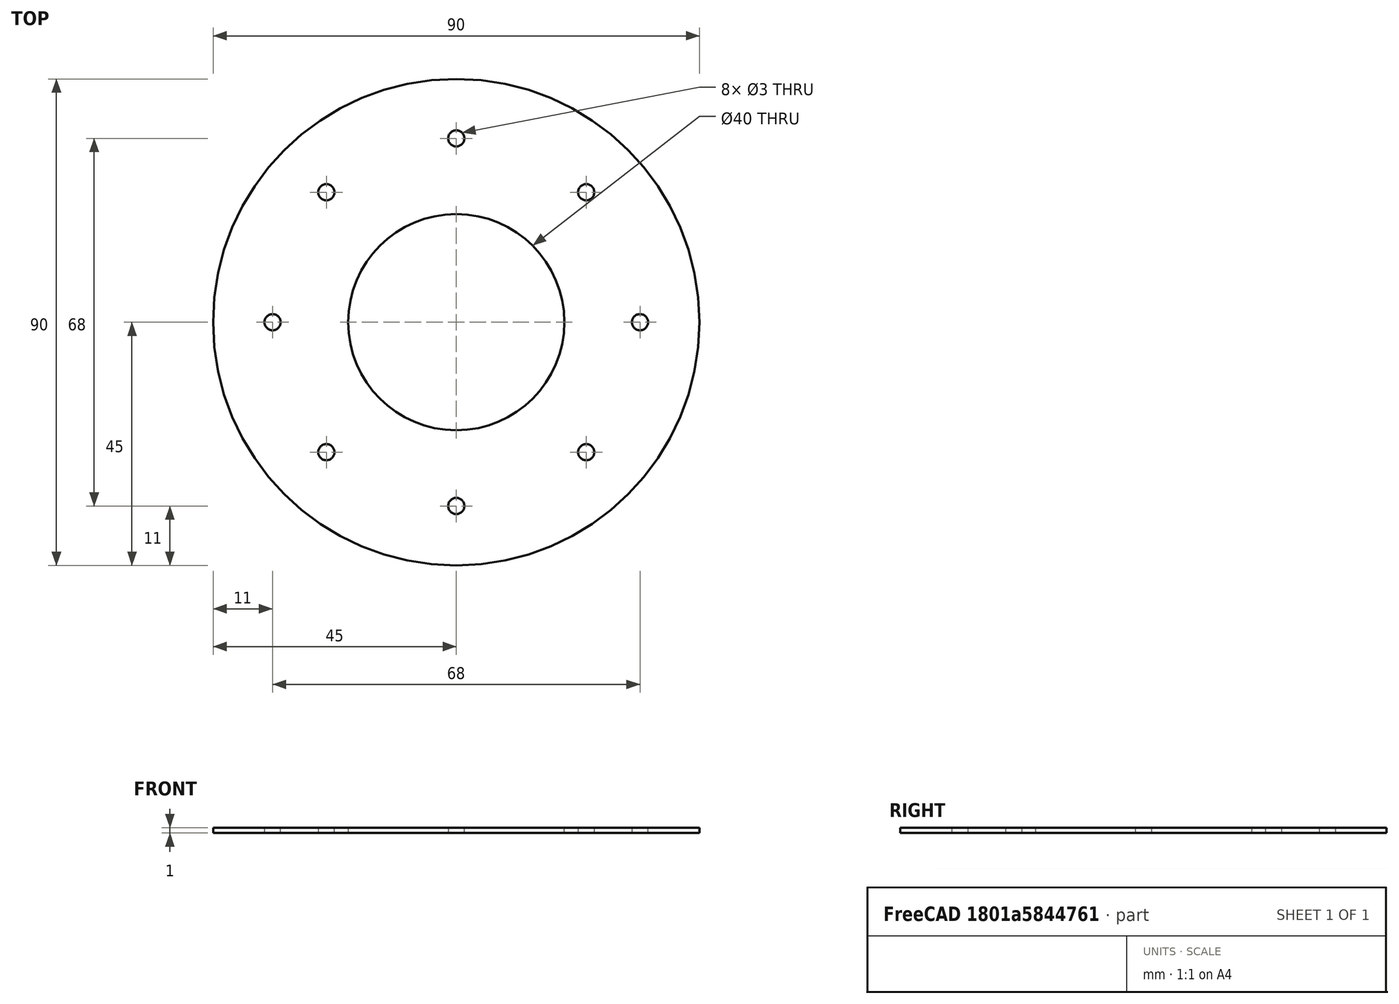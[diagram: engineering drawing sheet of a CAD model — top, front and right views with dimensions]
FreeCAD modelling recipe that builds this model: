
FCSTD DOCUMENT  (FreeCAD 0.20R29603 (Git))
Label: Rubber_Ring_I_LightDome
License: All rights reserved
LicenseURL: http://en.wikipedia.org/wiki/All_rights_reserved
objects: TechDraw::DrawViewDimension×4, App::DocumentObjectGroup×4, Sketcher::SketchObject×1, Part::Extrusion×1, TechDraw::DrawSVGTemplate×1, TechDraw::DrawViewPart×1, TechDraw::DrawViewAnnotation×1, TechDraw::DrawPage×1, App::Part×1
note: 2 computed .brp shape members not serialized (recipe doc carries the construction recipe); baked Part::Feature solids carry a one-line shape summary decoded from their .brp

FEATURE [Sketcher::SketchObject] Sketch
  FullyConstrained = false
  sketch-geometry (18):
    g0: Circle CenterX=0 CenterY=8e-16 CenterZ=0 NormalX=0 NormalY=0 NormalZ=1 AngleXU=0 Radius=20
    g1: LineSegment StartX=-70 StartY=70 StartZ=0 EndX=70 EndY=70 EndZ=0
    g2: LineSegment StartX=70 StartY=70 StartZ=0 EndX=70 EndY=-70 EndZ=0
    g3: LineSegment StartX=70 StartY=-70 StartZ=0 EndX=-70 EndY=-70 EndZ=0
    g4: LineSegment StartX=-70 StartY=-70 StartZ=0 EndX=-70 EndY=70 EndZ=0
    g5: LineSegment StartX=-70 StartY=70 StartZ=0 EndX=70 EndY=-70 EndZ=0
    g6: LineSegment StartX=70 StartY=70 StartZ=0 EndX=-70 EndY=-70 EndZ=0
    g7: GeomPoint X=0 Y=8e-16 Z=0
    g8: Circle CenterX=0 CenterY=8e-16 CenterZ=0 NormalX=0 NormalY=0 NormalZ=1 AngleXU=0 Radius=34
    g9: Circle CenterX=0 CenterY=8e-16 CenterZ=0 NormalX=0 NormalY=0 NormalZ=1 AngleXU=0 Radius=45
    g10: Circle CenterX=-24.0416 CenterY=24.0416 CenterZ=0 NormalX=0 NormalY=0 NormalZ=1 AngleXU=0 Radius=1.5
    g11: Circle CenterX=0 CenterY=34 CenterZ=0 NormalX=0 NormalY=0 NormalZ=1 AngleXU=0 Radius=1.5
    g12: Circle CenterX=34 CenterY=0 CenterZ=0 NormalX=0 NormalY=0 NormalZ=1 AngleXU=0 Radius=1.5
    g13: Circle CenterX=0 CenterY=-34 CenterZ=0 NormalX=0 NormalY=0 NormalZ=1 AngleXU=0 Radius=1.5
    g14: Circle CenterX=-24.0416 CenterY=-24.0416 CenterZ=0 NormalX=0 NormalY=0 NormalZ=1 AngleXU=0 Radius=1.5
    g15: Circle CenterX=-34 CenterY=0 CenterZ=0 NormalX=0 NormalY=0 NormalZ=1 AngleXU=0 Radius=1.5
    g16: Circle CenterX=24.0416 CenterY=-24.0416 CenterZ=0 NormalX=0 NormalY=0 NormalZ=1 AngleXU=0 Radius=1.5
    g17: Circle CenterX=24.0416 CenterY=24.0416 CenterZ=0 NormalX=0 NormalY=0 NormalZ=1 AngleXU=0 Radius=1.5
  constraints (49):
    c: Coincident(g0,g-1)
    c: Radius(g0) = 20
    c: Coincident(g1,g2)
    c: Coincident(g2,g3)
    c: Coincident(g3,g4)
    c: Coincident(g4,g1)
    c: Horizontal(g1)
    c: Horizontal(g3)
    c: Vertical(g2)
    c: Vertical(g4)
    c: PointOnObject(g7,g5)
    c: PointOnObject(g7,g6)
    c: Coincident(g6,g1)
    c: Coincident(g5,g1)
    c: Coincident(g6,g3)
    c: Coincident(g5,g2)
    c: Coincident(g7,g0)
    c: Equal(g1,g4)
    c: Equal(g4,g2)
    c: Equal(g2,g3)
    c: DistanceX(g1,g1) = 140
    c: Radius(g8) = 34
    c: Coincident(g8,g0)
    c: Radius(g9) = 45
    c: Coincident(g9,g0)
    c: Radius(g10) = 1.5
    c: PointOnObject(g10,g8)
    c: PointOnObject(g10,g5)
    c: Radius(g11) = 1.5
    c: PointOnObject(g11,g-2)
    c: PointOnObject(g11,g8)
    c: Radius(g17) = 1.5
    c: PointOnObject(g17,g6)
    c: PointOnObject(g17,g8)
    c: Radius(g12) = 1.5
    c: PointOnObject(g12,g-1)
    c: PointOnObject(g12,g8)
    c: Radius(g16) = 1.5
    c: PointOnObject(g16,g5)
    c: PointOnObject(g16,g8)
    c: Radius(g13) = 1.5
    c: PointOnObject(g13,g-2)
    c: PointOnObject(g13,g8)
    c: Radius(g14) = 1.5
    c: PointOnObject(g14,g6)
    c: PointOnObject(g14,g8)
    c: Radius(g15) = 1.5
    c: PointOnObject(g15,g-1)
    c: PointOnObject(g15,g8)
FEATURE [Part::Extrusion] Extrude
  Base = -> Sketch
  Dir = (0,0,1)
  DirMode = 2
  FaceMakerClass = Part::FaceMakerBullseye
  LengthFwd = 1
  LengthRev = 0
  Solid = true
  Symmetric = false
FEATURE [TechDraw::DrawSVGTemplate] Template
  EditableTexts = AUTHOR_NAME=Norman Rembarz,DN=1,DRAWING_TITLE=REGREEN - SensoLAB,FC-DATE=28/10/2020,FC-REV=REV A,FC-SC=1:1,FC-SH=1,FC-SI=A4,+4 more (map truncated)
  Height = 210
  Orientation = 1
  Width = 297
FEATURE [TechDraw::DrawViewPart] View
  CoarseView = false
  Direction = (0,0,0.12)
  Focus = 100
  HardHidden = false
  IsoCount = 0
  IsoHidden = false
  IsoVisible = false
  LockPosition = false
  Perspective = false
  Rotation = 0
  ScaleType = 0
  SeamHidden = false
  SeamVisible = false
  SmoothHidden = false
  SmoothVisible = false
  Source = -> [Extrude]
  X = 138.628
  XDirection = (1,0,0)
  Y = 119.128
FEATURE [TechDraw::DrawViewDimension] Dimension
  AngleOverride = false
  Arbitrary = false
  ArbitraryTolerances = false
  EqualTolerance = false
  ExtensionAngle = 0
  FormatSpec = ⌀%.2f
  FormatSpecOverTolerance = %+.2w
  FormatSpecUnderTolerance = %+.2w
  Inverted = false
  LineAngle = 0
  LockPosition = false
  MeasureType = 1
  OverTolerance = 0
  References2D = -> [View]
  Rotation = 0
  ScaleType = 0
  TheoreticalExact = false
  Type = 5
  UnderTolerance = 0
  X = -80.8511
  Y = 32.1277
FEATURE [TechDraw::DrawViewDimension] Dimension001
  AngleOverride = false
  Arbitrary = false
  ArbitraryTolerances = false
  EqualTolerance = false
  ExtensionAngle = 0
  FormatSpec = ⌀%.2f
  FormatSpecOverTolerance = %+.2w
  FormatSpecUnderTolerance = %+.2w
  Inverted = false
  LineAngle = 0
  LockPosition = false
  MeasureType = 1
  OverTolerance = 0
  References2D = -> [View]
  Rotation = 0
  ScaleType = 0
  TheoreticalExact = false
  Type = 5
  UnderTolerance = 0
  X = -89.7872
  Y = 47.8723
FEATURE [TechDraw::DrawViewDimension] Dimension002
  AngleOverride = false
  Arbitrary = false
  ArbitraryTolerances = false
  EqualTolerance = false
  ExtensionAngle = 0
  FormatSpec = ⌀%.2f
  FormatSpecOverTolerance = %+.2w
  FormatSpecUnderTolerance = %+.2w
  Inverted = false
  LineAngle = 0
  LockPosition = false
  MeasureType = 1
  OverTolerance = 0
  References2D = -> [View]
  Rotation = 0
  ScaleType = 0
  TheoreticalExact = false
  Type = 5
  UnderTolerance = 0
  X = 53.6824
  Y = 55.301
FEATURE [TechDraw::DrawViewDimension] Dimension003
  AngleOverride = false
  Arbitrary = false
  ArbitraryTolerances = false
  EqualTolerance = false
  ExtensionAngle = 0
  FormatSpec = %.2f
  FormatSpecOverTolerance = %+.2w
  FormatSpecUnderTolerance = %+.2w
  Inverted = false
  LineAngle = 0
  LockPosition = false
  MeasureType = 1
  OverTolerance = 0
  References2D = -> [View]
  Rotation = 0
  ScaleType = 0
  TheoreticalExact = false
  Type = 0
  UnderTolerance = 0
  X = 1.03757
  Y = -9.39893
FEATURE [TechDraw::DrawViewAnnotation] Annotation
  Font = osifont
  LineSpace = 80
  LockPosition = false
  MaxWidth = -1
  Rotation = 0
  ScaleType = 0
  Text = thickness of rubber material | should be 1mm
  TextSize = 5
  TextStyle = 0
  X = 239.649
  Y = 77.6809
FEATURE [TechDraw::DrawPage] Page
  KeepUpdated = true
  NextBalloonIndex = 1
  ProjectionType = 0
  Template = -> Template
  Views = -> [View,Dimension,Dimension001,Dimension002,Dimension003,Annotation]
FEATURE [App::DocumentObjectGroup] Group
FEATURE [App::DocumentObjectGroup] Group001
FEATURE [App::DocumentObjectGroup] Group002
FEATURE [App::DocumentObjectGroup] Group003
FEATURE [App::Part] Part
  Origin = -> Origin
